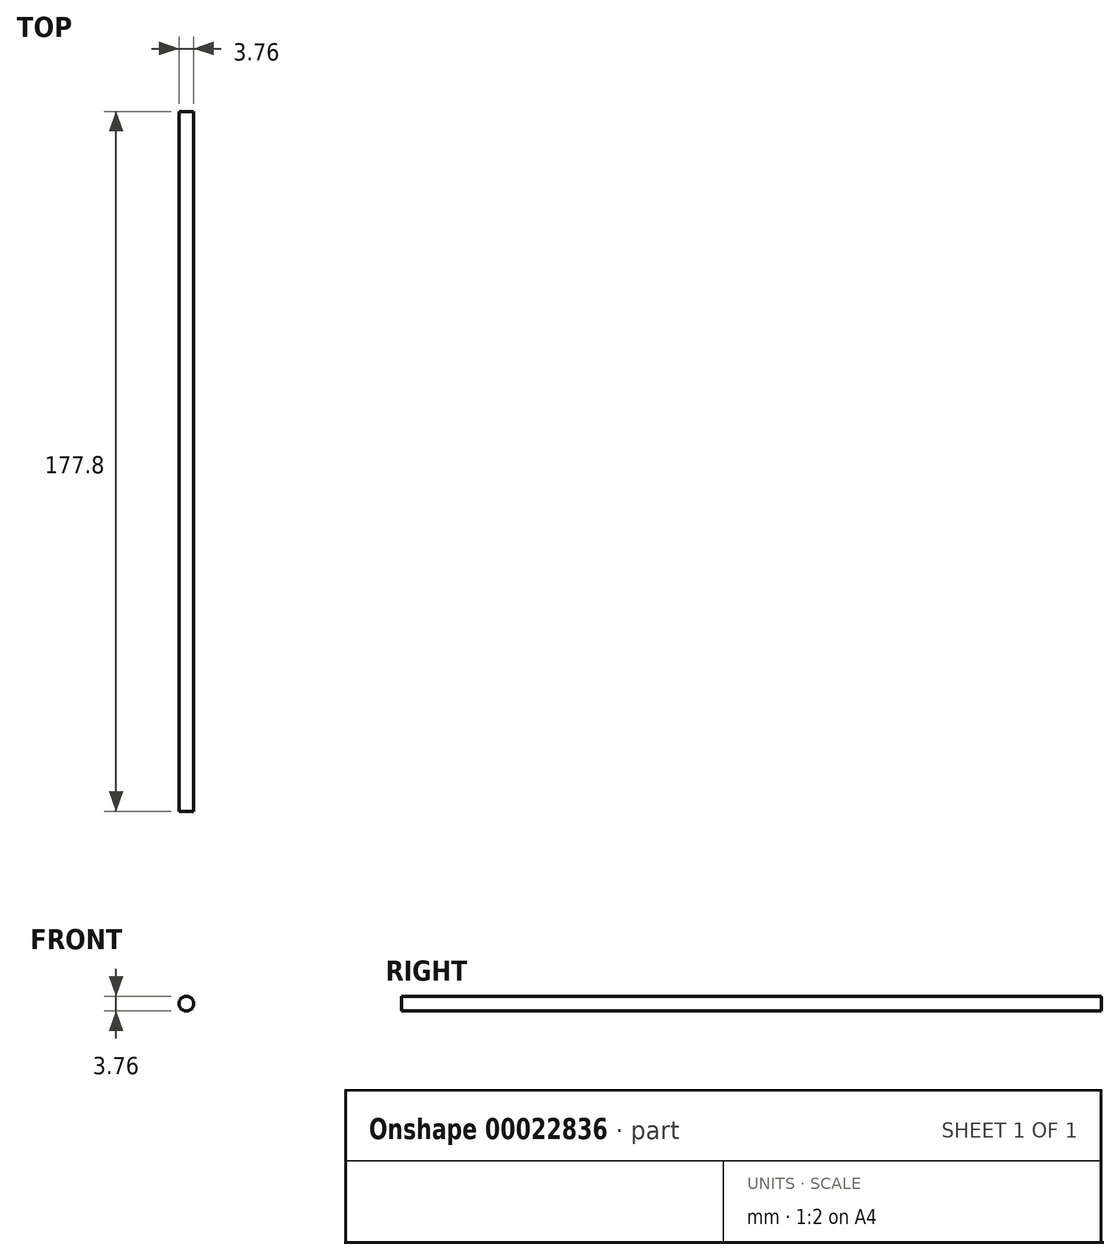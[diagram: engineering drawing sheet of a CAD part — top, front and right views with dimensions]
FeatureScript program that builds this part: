
annotation { "Feature Type Name" : "Feature", "Feature Type Description" : "" }
export const myFeature = defineFeature(function(context is Context, id is Id, definition is map)
    precondition{}
    {
        {
            var Q0;
            Q0=qCreatedBy(makeId("Front.planeOp"),FACE);
            var sketch = newSketch(context, id + "F0", { "sketchPlane" : qUnion([Q0])});
            skCircle(sketch, "E0", {"center": v(0, 0) * mm, "radius": 1.88 * mm});
            skSolve(sketch);
        }
        {
            var Q0;
            Q0=makeQuery(id+"F0.imprint","IMPRINT",FACE,{"disambiguationData":[TD([[makeQuery(id+"F0.imprint","IMPRINT",EDGE,{"derivedFrom":sQuery(id+"F0.wireOp",EDGE,"E0")}),1.0]])]});
            extrude(context, id + "F1", {"entities" : qUnion([Q0]), "oppositeDirection" : true, "depth" : 177.8 * mm});
        }
    });
